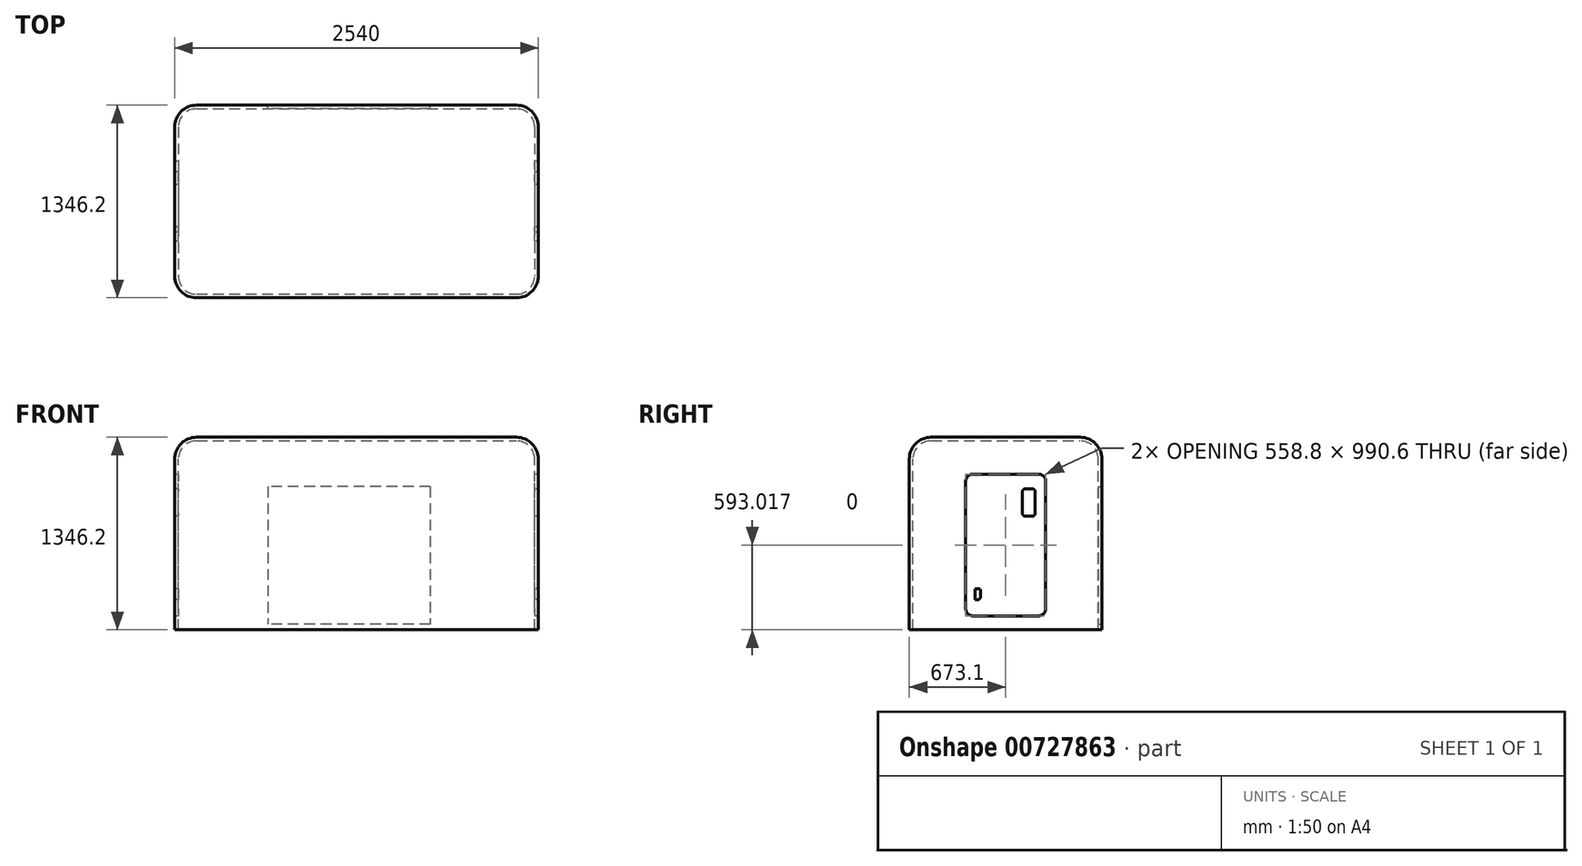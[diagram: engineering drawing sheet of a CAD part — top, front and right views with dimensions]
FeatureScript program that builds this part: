
annotation { "Feature Type Name" : "Feature", "Feature Type Description" : "" }
export const myFeature = defineFeature(function(context is Context, id is Id, definition is map)
    precondition{}
    {
        {
            var Q0;
            Q0=qCreatedBy(makeId("Top.planeOp"),FACE);
            var sketch = newSketch(context, id + "F0", { "sketchPlane" : qUnion([Q0])});
            skLineSegment(sketch, "E0.bottom", {"start": v(-1229.77, 673.1) * mm, "end": v(1310.23, 673.1) * mm});
            skLineSegment(sketch, "E0.top", {"start": v(-1229.77, -673.1) * mm, "end": v(1310.23, -673.1) * mm});
            skLineSegment(sketch, "E0.left", {"start": v(-1229.77, 673.1) * mm, "end": v(-1229.77, -673.1) * mm});
            skLineSegment(sketch, "E0.right", {"start": v(1310.23, 673.1) * mm, "end": v(1310.23, -673.1) * mm});
            skPoint(sketch, "E0.middle", {"position": v(40.23, 0) * mm});
            skSolve(sketch);
        }
        {
            var Q0;
            Q0 = qSketchRegion(id + "F0", true);
            extrude(context, id + "F1", {"entities" : qUnion([Q0]), "depth" : 1346.2 * mm, "offsetDistance" : 25.4 * mm});
        }
        {
            var Q0;
            Q0=makeQuery(id+"F1.opExtrude","SWEPT_EDGE",EDGE,{"disambiguationData":[OSD([sQuery(id+"F0.wireOp",EDGE,"E0.bottom"),sQuery(id+"F0.wireOp",EDGE,"E0.left")])]});
            var Q1;
            Q1=makeQuery(id+"F1.opExtrude","CAP_EDGE",EDGE,{"disambiguationData":[OSD([sQuery(id+"F0.wireOp",EDGE,"E0.left")])],"isStart":false});
            var Q2;
            Q2=makeQuery(id+"F1.opExtrude","SWEPT_EDGE",EDGE,{"disambiguationData":[OSD([sQuery(id+"F0.wireOp",EDGE,"E0.top"),sQuery(id+"F0.wireOp",EDGE,"E0.left")])]});
            var Q3;
            Q3=makeQuery(id+"F1.opExtrude","CAP_EDGE",EDGE,{"disambiguationData":[OSD([sQuery(id+"F0.wireOp",EDGE,"E0.top")])],"isStart":false});
            var Q4;
            Q4=makeQuery(id+"F1.opExtrude","CAP_EDGE",EDGE,{"disambiguationData":[OSD([sQuery(id+"F0.wireOp",EDGE,"E0.right")])],"isStart":false});
            var Q5;
            Q5=makeQuery(id+"F1.opExtrude","SWEPT_EDGE",EDGE,{"disambiguationData":[OSD([sQuery(id+"F0.wireOp",EDGE,"E0.top"),sQuery(id+"F0.wireOp",EDGE,"E0.right")])]});
            var Q6;
            Q6=makeQuery(id+"F1.opExtrude","SWEPT_EDGE",EDGE,{"disambiguationData":[OSD([sQuery(id+"F0.wireOp",EDGE,"E0.bottom"),sQuery(id+"F0.wireOp",EDGE,"E0.right")])]});
            var Q7;
            Q7=makeQuery(id+"F1.opExtrude","CAP_EDGE",EDGE,{"disambiguationData":[OSD([sQuery(id+"F0.wireOp",EDGE,"E0.bottom")])],"isStart":false});
            fillet(context, id + "F2", {"entities" : qUnion([Q0, Q1, Q2, Q3, Q4, Q5, Q6, Q7]), "radius" : 152.4 * mm, "tangentPropagation" : true, "allowEdgeOverflow" : false});
        }
        {
            var Q0;
            Q0=makeQuery(id+"F1.opExtrude","CAP_FACE",FACE,{"disambiguationData":[OSD([sQuery(id+"F0.wireOp",EDGE,"E0.bottom"),sQuery(id+"F0.wireOp",EDGE,"E0.top"),sQuery(id+"F0.wireOp",EDGE,"E0.left"),sQuery(id+"F0.wireOp",EDGE,"E0.right")])],"isStart":true});
            shell(context, id + "F3", {"entities" : qUnion([Q0]), "thickness" : 25.4 * mm});
        }
        {
            var Q0;
            Q0=makeQuery(id+"F1.opExtrude","SWEPT_FACE",FACE,{"disambiguationData":[OSD([sQuery(id+"F0.wireOp",EDGE,"E0.left")])]});
            var sketch = newSketch(context, id + "F4", { "sketchPlane" : qUnion([Q0])});
            skLineSegment(sketch, "E1.bottom", {"start": v(228.6, 1088.32) * mm, "end": v(-228.6, 1088.32) * mm});
            skLineSegment(sketch, "E1.top", {"start": v(228.6, 97.72) * mm, "end": v(-228.6, 97.72) * mm});
            skLineSegment(sketch, "E1.left", {"start": v(279.4, 1037.52) * mm, "end": v(279.4, 148.52) * mm});
            skLineSegment(sketch, "E1.right", {"start": v(-279.4, 1037.52) * mm, "end": v(-279.4, 148.52) * mm});
            skPoint(sketch, "E1.middle", {"position": v(0, 593.02) * mm});
            skPoint(sketch, "E2.visualSharp", {"position": v(-279.4, 1088.32) * mm});
            skArc(sketch, "E2.filletArc", {"start": v(-228.6, 1088.32) * mm, "mid": v(-264.52, 1073.44) * mm, "end": v(-279.4, 1037.52) * mm});
            skPoint(sketch, "E3.visualSharp", {"position": v(279.4, 1088.32) * mm});
            skArc(sketch, "E3.filletArc", {"start": v(279.4, 1037.52) * mm, "mid": v(264.52, 1073.44) * mm, "end": v(228.6, 1088.32) * mm});
            skPoint(sketch, "E4.visualSharp", {"position": v(279.4, 97.72) * mm});
            skArc(sketch, "E4.filletArc", {"start": v(228.6, 97.72) * mm, "mid": v(264.52, 112.6) * mm, "end": v(279.4, 148.52) * mm});
            skPoint(sketch, "E5.visualSharp", {"position": v(-279.4, 97.72) * mm});
            skArc(sketch, "E5.filletArc", {"start": v(-279.4, 148.52) * mm, "mid": v(-264.52, 112.6) * mm, "end": v(-228.6, 97.72) * mm});
            skLineSegment(sketch, "E6.bottom", {"start": v(195.02, 211.32) * mm, "end": v(214.07, 211.32) * mm});
            skLineSegment(sketch, "E6.top", {"start": v(188.67, 287.52) * mm, "end": v(214.07, 287.52) * mm});
            skLineSegment(sketch, "E6.left", {"start": v(175.97, 230.37) * mm, "end": v(175.97, 274.82) * mm});
            skLineSegment(sketch, "E6.right", {"start": v(214.07, 211.32) * mm, "end": v(214.07, 287.52) * mm});
            skPoint(sketch, "E6.middle", {"position": v(195.02, 249.42) * mm});
            skLineSegment(sketch, "E7.bottom", {"start": v(-187.3, 985.4) * mm, "end": v(-136.5, 985.4) * mm});
            skLineSegment(sketch, "E7.top", {"start": v(-187.3, 794.9) * mm, "end": v(-136.5, 794.9) * mm});
            skLineSegment(sketch, "E7.left", {"start": v(-206.34, 966.34) * mm, "end": v(-206.34, 813.94) * mm});
            skLineSegment(sketch, "E7.right", {"start": v(-117.44, 966.34) * mm, "end": v(-117.44, 813.94) * mm});
            skPoint(sketch, "E8.visualSharp", {"position": v(-206.34, 985.4) * mm});
            skArc(sketch, "E8.filletArc", {"start": v(-187.3, 985.4) * mm, "mid": v(-200.76, 979.81) * mm, "end": v(-206.34, 966.34) * mm});
            skPoint(sketch, "E9.visualSharp", {"position": v(-117.44, 985.4) * mm});
            skArc(sketch, "E9.filletArc", {"start": v(-117.44, 966.34) * mm, "mid": v(-123.02, 979.81) * mm, "end": v(-136.5, 985.4) * mm});
            skPoint(sketch, "E10.visualSharp", {"position": v(-117.44, 794.9) * mm});
            skArc(sketch, "E10.filletArc", {"start": v(-136.5, 794.9) * mm, "mid": v(-123.02, 800.47) * mm, "end": v(-117.44, 813.94) * mm});
            skPoint(sketch, "E11.visualSharp", {"position": v(-206.34, 794.9) * mm});
            skArc(sketch, "E11.filletArc", {"start": v(-206.34, 813.94) * mm, "mid": v(-200.76, 800.47) * mm, "end": v(-187.3, 794.9) * mm});
            skPoint(sketch, "E12.visualSharp", {"position": v(175.97, 287.52) * mm});
            skArc(sketch, "E12.filletArc", {"start": v(188.67, 287.52) * mm, "mid": v(179.7, 283.8) * mm, "end": v(175.97, 274.82) * mm});
            skPoint(sketch, "E13.visualSharp", {"position": v(175.97, 211.32) * mm});
            skArc(sketch, "E13.filletArc", {"start": v(175.97, 230.37) * mm, "mid": v(181.55, 216.9) * mm, "end": v(195.02, 211.32) * mm});
            skSolve(sketch);
        }
        {
            var Q0;
            Q0=makeQuery(id+"F4.imprint","IMPRINT",FACE,{"disambiguationData":[TD([[makeQuery(id+"F4.imprint","IMPRINT",EDGE,{"derivedFrom":sQuery(id+"F4.wireOp",EDGE,"E1.bottom")}),1.0]])]});
            extrude(context, id + "F5", {"entities" : qUnion([Q0]), "operationType" : NewBodyOperationType.REMOVE, "oppositeDirection" : true, "depth" : 3449.32 * mm, "offsetDistance" : 25.4 * mm});
        }
        {
            var Q0;
            Q0=makeQuery(id+"F1.opExtrude","SWEPT_FACE",FACE,{"disambiguationData":[OSD([sQuery(id+"F0.wireOp",EDGE,"E0.bottom")])]});
            var sketch = newSketch(context, id + "F6", { "sketchPlane" : qUnion([Q0])});
            skLineSegment(sketch, "E14.bottom", {"start": v(-555.63, 1000.34) * mm, "end": v(578.8, 1000.34) * mm});
            skLineSegment(sketch, "E14.top", {"start": v(-555.63, 39.2) * mm, "end": v(578.8, 39.2) * mm});
            skLineSegment(sketch, "E14.left", {"start": v(-555.63, 1000.34) * mm, "end": v(-555.63, 39.2) * mm});
            skLineSegment(sketch, "E14.right", {"start": v(578.8, 1000.34) * mm, "end": v(578.8, 39.2) * mm});
            skSolve(sketch);
        }
        {
            var Q0;
            Q0=makeQuery(id+"F6.imprint","IMPRINT",FACE,{"disambiguationData":[TD([[makeQuery(id+"F6.imprint","IMPRINT",EDGE,{"derivedFrom":sQuery(id+"F6.wireOp",EDGE,"E14.bottom")}),-1.0]])]});
            extrude(context, id + "F7", {"entities" : qUnion([Q0]), "operationType" : NewBodyOperationType.REMOVE, "oppositeDirection" : true, "depth" : 25.4 * mm, "offsetDistance" : 25.4 * mm});
        }
    });
